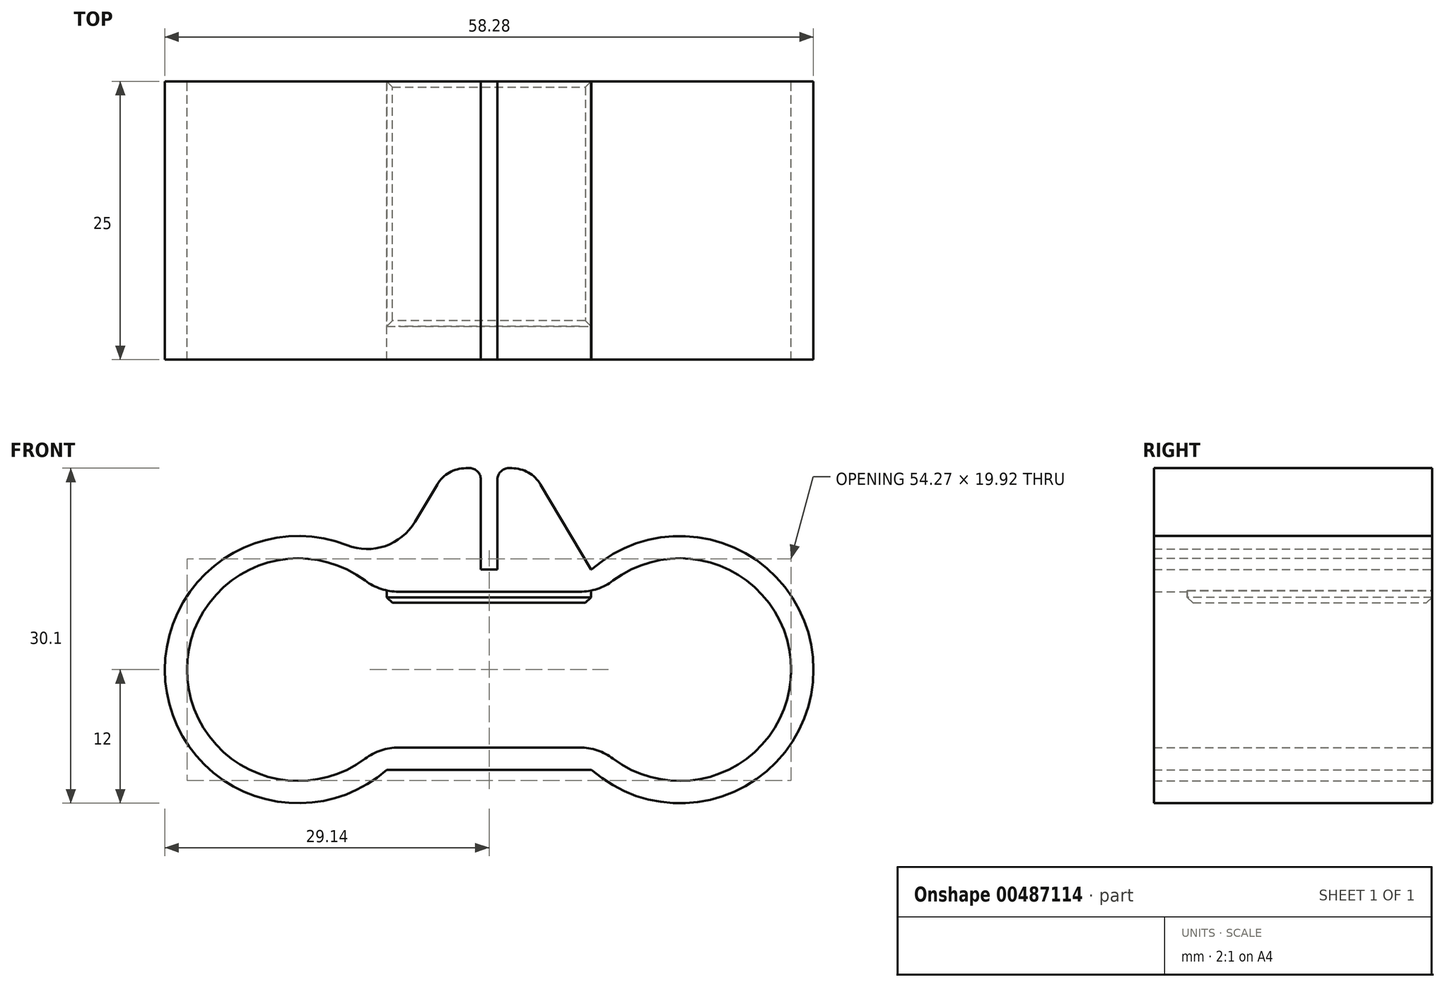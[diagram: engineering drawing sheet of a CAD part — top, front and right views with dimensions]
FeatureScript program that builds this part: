
annotation { "Feature Type Name" : "Feature", "Feature Type Description" : "" }
export const myFeature = defineFeature(function(context is Context, id is Id, definition is map)
    precondition{}
    {
        {
            var Q0;
            Q0=qCreatedBy(makeId("Front.planeOp"),FACE);
            var sketch = newSketch(context, id + "F0", { "sketchPlane" : qUnion([Q0])});
            skLineSegment(sketch, "E0", {"start": v(-17.14, 0) * mm, "end": v(17.14, 0) * mm, "construction": true});
            skArc(sketch, "E1", {"start": v(-10, 7) * mm, "mid": v(-27.14, 0) * mm, "end": v(-10, -7) * mm});
            skArc(sketch, "E2", {"start": v(10, -7) * mm, "mid": v(27.14, 0) * mm, "end": v(10, 7) * mm});
            skLineSegment(sketch, "E3", {"start": v(-10, -7) * mm, "end": v(10, -7) * mm});
            skLineSegment(sketch, "E4", {"start": v(-10, 7) * mm, "end": v(10, 7) * mm});
            skArc(sketch, "E5.0", {"start": v(-9.2, 9) * mm, "mid": v(-29.14, 0) * mm, "end": v(-9.2, -9) * mm});
            skLineSegment(sketch, "E5.1", {"start": v(-9.2, 9) * mm, "end": v(9.2, 9) * mm});
            skArc(sketch, "E5.2", {"start": v(9.2, -9) * mm, "mid": v(29.14, 0) * mm, "end": v(9.2, 9) * mm});
            skLineSegment(sketch, "E5.3", {"start": v(-9.2, -9) * mm, "end": v(9.2, -9) * mm});
            skSolve(sketch);
        }
        {
            var Q0;
            Q0=qCreatedBy(makeId("Front.planeOp"),FACE);
            var sketch = newSketch(context, id + "F1", { "sketchPlane" : qUnion([Q0])});
            skArc(sketch, "E6.0.0", {"start": v(-9.2, 9) * mm, "mid": v(-29.14, 0) * mm, "end": v(-9.2, -9) * mm});
            skLineSegment(sketch, "E6.0.1", {"start": v(-9.2, -9) * mm, "end": v(9.2, -9) * mm});
            skArc(sketch, "E6.0.2", {"start": v(9.2, -9) * mm, "mid": v(29.14, 0) * mm, "end": v(9.2, 9) * mm});
            skLineSegment(sketch, "E6.0.3", {"start": v(9.2, 9) * mm, "end": v(-9.2, 9) * mm});
            skLineSegment(sketch, "E7.0.0", {"start": v(-10, -7) * mm, "end": v(10, -7) * mm});
            skArc(sketch, "E7.0.1", {"start": v(10, -7) * mm, "mid": v(27.14, 0) * mm, "end": v(10, 7) * mm});
            skLineSegment(sketch, "E7.0.2", {"start": v(10, 7) * mm, "end": v(-10, 7) * mm});
            skArc(sketch, "E7.0.3", {"start": v(-10, 7) * mm, "mid": v(-27.14, 0) * mm, "end": v(-10, -7) * mm});
            skLineSegment(sketch, "E8", {"start": v(-0.75, 9) * mm, "end": v(-0.75, 18.1) * mm});
            skLineSegment(sketch, "E9", {"start": v(0.75, 9) * mm, "end": v(0.75, 18.1) * mm});
            skLineSegment(sketch, "E10", {"start": v(-0.75, 9) * mm, "end": v(0.75, 9) * mm});
            skPoint(sketch, "E11", {"position": v(0, 9) * mm});
            skLineSegment(sketch, "E12", {"start": v(4.62, 16.63) * mm, "end": v(9.17, 8.97) * mm});
            skLineSegment(sketch, "E13", {"start": v(-4.67, 16.63) * mm, "end": v(-9.2, 9) * mm});
            skLineSegment(sketch, "E14", {"start": v(-0.75, 18.1) * mm, "end": v(-2.1, 18.1) * mm});
            skLineSegment(sketch, "E15", {"start": v(0.75, 18.1) * mm, "end": v(2.04, 18.1) * mm});
            skPoint(sketch, "E16.visualSharp", {"position": v(-3.8, 18.1) * mm});
            skArc(sketch, "E16.filletArc", {"start": v(-2.1, 18.1) * mm, "mid": v(-3.58, 17.7) * mm, "end": v(-4.67, 16.63) * mm});
            skPoint(sketch, "E17.visualSharp", {"position": v(3.75, 18.1) * mm});
            skArc(sketch, "E17.filletArc", {"start": v(4.62, 16.63) * mm, "mid": v(3.53, 17.7) * mm, "end": v(2.04, 18.1) * mm});
            skSolve(sketch);
        }
        {
            var Q0;
            {var subQ8=sQuery(id+"F1.wireOp",EDGE,"E6.0.1");Q0=makeQuery(id+"F1.imprint","IMPRINT",FACE,{"disambiguationData":[TD([[makeQuery(id+"F1.imprint","IMPRINT",EDGE,{"derivedFrom":subQ8}),1.0]])]});}
            extrude(context, id + "F2", {"entities" : qUnion([Q0]), "depth" : 25 * mm});
        }
        {
            var Q0;
            Q0=qCreatedBy(makeId("Front.planeOp"),FACE);
            var sketch = newSketch(context, id + "F3", { "sketchPlane" : qUnion([Q0])});
            skArc(sketch, "E18.0.0", {"start": v(-2.1, 18.1) * mm, "mid": v(-3.58, 17.7) * mm, "end": v(-4.67, 16.63) * mm});
            skLineSegment(sketch, "E18.0.1", {"start": v(-4.67, 16.63) * mm, "end": v(-9.2, 9) * mm});
            skLineSegment(sketch, "E18.0.3", {"start": v(-0.75, 9) * mm, "end": v(-0.75, 18.1) * mm});
            skLineSegment(sketch, "E18.0.4", {"start": v(-0.75, 18.1) * mm, "end": v(-2.1, 18.1) * mm});
            skLineSegment(sketch, "E19.0.0", {"start": v(9.15, 9) * mm, "end": v(4.62, 16.63) * mm});
            skArc(sketch, "E19.0.1", {"start": v(4.62, 16.63) * mm, "mid": v(3.53, 17.7) * mm, "end": v(2.04, 18.1) * mm});
            skLineSegment(sketch, "E19.0.2", {"start": v(2.04, 18.1) * mm, "end": v(0.75, 18.1) * mm});
            skLineSegment(sketch, "E19.0.3", {"start": v(0.75, 18.1) * mm, "end": v(0.75, 9) * mm});
            skLineSegment(sketch, "E20", {"start": v(-9.2, 9) * mm, "end": v(-9.2, 6) * mm});
            skLineSegment(sketch, "E21", {"start": v(-9.2, 6) * mm, "end": v(9.15, 6) * mm});
            skLineSegment(sketch, "E22", {"start": v(9.15, 6) * mm, "end": v(9.15, 9) * mm});
            skLineSegment(sketch, "E23", {"start": v(0.75, 9) * mm, "end": v(-0.75, 9) * mm});
            skSolve(sketch);
        }
        {
            var Q0;
            Q0 = qSketchRegion(id + "F3", true);
            extrude(context, id + "F4", {"entities" : qUnion([Q0]), "depth" : 22 * mm, "offsetDistance" : 25 * mm});
        }
        {
            var Q0;
            Q0=makeQuery(id+"F4.opExtrude","SWEPT_EDGE",EDGE,{"disambiguationData":[OSD([sQuery(id+"F3.wireOp",EDGE,"E19.0.0"),sQuery(id+"F3.wireOp",EDGE,"E22")])]});
            var Q1;
            Q1=makeQuery(id+"F4.opExtrude","SWEPT_EDGE",EDGE,{"disambiguationData":[OSD([sQuery(id+"F3.wireOp",EDGE,"E18.0.1"),sQuery(id+"F3.wireOp",EDGE,"E20")])]});
            fillet(context, id + "F5", {"entities" : qUnion([Q0, Q1]), "radius" : 5 * mm, "tangentPropagation" : true, "allowEdgeOverflow" : false});
        }
        {
            var Q0;
            Q0=makeQuery(id+"F4.opExtrude","SWEPT_EDGE",EDGE,{"disambiguationData":[OSD([sQuery(id+"F3.wireOp",EDGE,"E18.0.3"),sQuery(id+"F3.wireOp",EDGE,"E18.0.4")])]});
            var Q1;
            Q1=makeQuery(id+"F4.opExtrude","SWEPT_EDGE",EDGE,{"disambiguationData":[OSD([sQuery(id+"F3.wireOp",EDGE,"E19.0.2"),sQuery(id+"F3.wireOp",EDGE,"E19.0.3")])]});
            fillet(context, id + "F6", {"entities" : qUnion([Q0, Q1]), "radius" : .5 * mm, "tangentPropagation" : true, "allowEdgeOverflow" : false});
        }
        {
            var Q0;
            Q0=makeQuery(id+"F4.opExtrude","SWEPT_FACE",FACE,{"disambiguationData":[OSD([sQuery(id+"F3.wireOp",EDGE,"E21")])]});
            chamfer(context, id + "F7", {"entities" : qUnion([Q0]), "width" : .5 * mm, "tangentPropagation" : true});
        }
        {
            var Q0;
            {var subQ4=sQuery(id+"F1.wireOp",EDGE,"E9");Q0=makeQuery(id+"F1.imprint","IMPRINT",FACE,{"disambiguationData":[TD([[makeQuery(id+"F1.imprint","IMPRINT",EDGE,{"derivedFrom":subQ4}),-1.0]])]});}
            var Q1;
            {var subQ4=sQuery(id+"F1.wireOp",EDGE,"E8");Q1=makeQuery(id+"F1.imprint","IMPRINT",FACE,{"disambiguationData":[TD([[makeQuery(id+"F1.imprint","IMPRINT",EDGE,{"derivedFrom":subQ4}),1.0]])]});}
            extrude(context, id + "F8", {"entities" : qUnion([Q0, Q1]), "operationType" : NewBodyOperationType.ADD, "depth" : 25 * mm});
        }
        {
            var Q0;
            Q0=makeQuery(id+"F8.opExtrude","SWEPT_EDGE",EDGE,{"disambiguationData":[OSD([sQuery(id+"F1.wireOp",EDGE,"E6.0.0"),sQuery(id+"F1.wireOp",EDGE,"E13")])]});
            var Q1;
            Q1=makeQuery(id+"F8.opExtrude","SWEPT_EDGE",EDGE,{"disambiguationData":[OSD([sQuery(id+"F1.wireOp",EDGE,"E6.0.2"),sQuery(id+"F1.wireOp",EDGE,"E12")])]});
            var Q2;
            Q2=makeQuery(id+"F2.opExtrude","SWEPT_EDGE",EDGE,{"disambiguationData":[OSD([sQuery(id+"F1.wireOp",EDGE,"E7.0.2"),sQuery(id+"F1.wireOp",EDGE,"E7.0.3")])]});
            var Q3;
            Q3=makeQuery(id+"F2.opExtrude","SWEPT_EDGE",EDGE,{"disambiguationData":[OSD([sQuery(id+"F1.wireOp",EDGE,"E7.0.1"),sQuery(id+"F1.wireOp",EDGE,"E7.0.2")])]});
            var Q4;
            Q4=makeQuery(id+"F2.opExtrude","SWEPT_EDGE",EDGE,{"disambiguationData":[OSD([sQuery(id+"F1.wireOp",EDGE,"E7.0.0"),sQuery(id+"F1.wireOp",EDGE,"E7.0.3")])]});
            var Q5;
            Q5=makeQuery(id+"F2.opExtrude","SWEPT_EDGE",EDGE,{"disambiguationData":[OSD([sQuery(id+"F1.wireOp",EDGE,"E7.0.0"),sQuery(id+"F1.wireOp",EDGE,"E7.0.1")])]});
            fillet(context, id + "F9", {"entities" : qUnion([Q0, Q1, Q2, Q3, Q4, Q5]), "radius" : 5 * mm, "tangentPropagation" : true, "allowEdgeOverflow" : false});
        }
        {
            var Q0;
            Q0=makeQuery(id+"F8.opExtrude","SWEPT_EDGE",EDGE,{"disambiguationData":[OSD([sQuery(id+"F1.wireOp",EDGE,"E13"),sQuery(id+"F1.wireOp",EDGE,"E14")])]});
            var Q1;
            Q1=makeQuery(id+"F8.opExtrude","SWEPT_EDGE",EDGE,{"disambiguationData":[OSD([sQuery(id+"F1.wireOp",EDGE,"E12"),sQuery(id+"F1.wireOp",EDGE,"E15")])]});
            fillet(context, id + "F10", {"entities" : qUnion([Q0, Q1]), "radius" : 1 * mm, "tangentPropagation" : true, "allowEdgeOverflow" : false});
        }
    });
